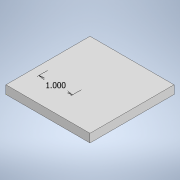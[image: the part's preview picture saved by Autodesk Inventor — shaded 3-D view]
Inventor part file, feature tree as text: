
AUTODESK INVENTOR PART (.ipt)
format: ipt  version: 2020 (Build 240168000, 168)  size: 163,840 bytes
history: native  units: in
note: dims shown in document units (in); Inventor stores cm internally (conversion verified against a paired STEP export)
features: sketch x3, extrude x1, emboss x1
ambient origin geometry x8: Origin, YZ Plane, XZ Plane, XY Plane, X Axis, Y Axis, Z Axis, Center Point
bodies: Solid1 (feature_tree)
feature tree (5):
  extrude  "Extrusion1"  Depth=2.5in
  emboss  "Emboss2"
  sketch  "Sketch5"  dims[d7=0.02in d8=0.0in d9=1.0in]
  sketch  "Sketch1"  dims[d0=2.5in d1=2.5in]
  sketch  "Sketch4"  dims[d2=0.25in d3=0.0in]
